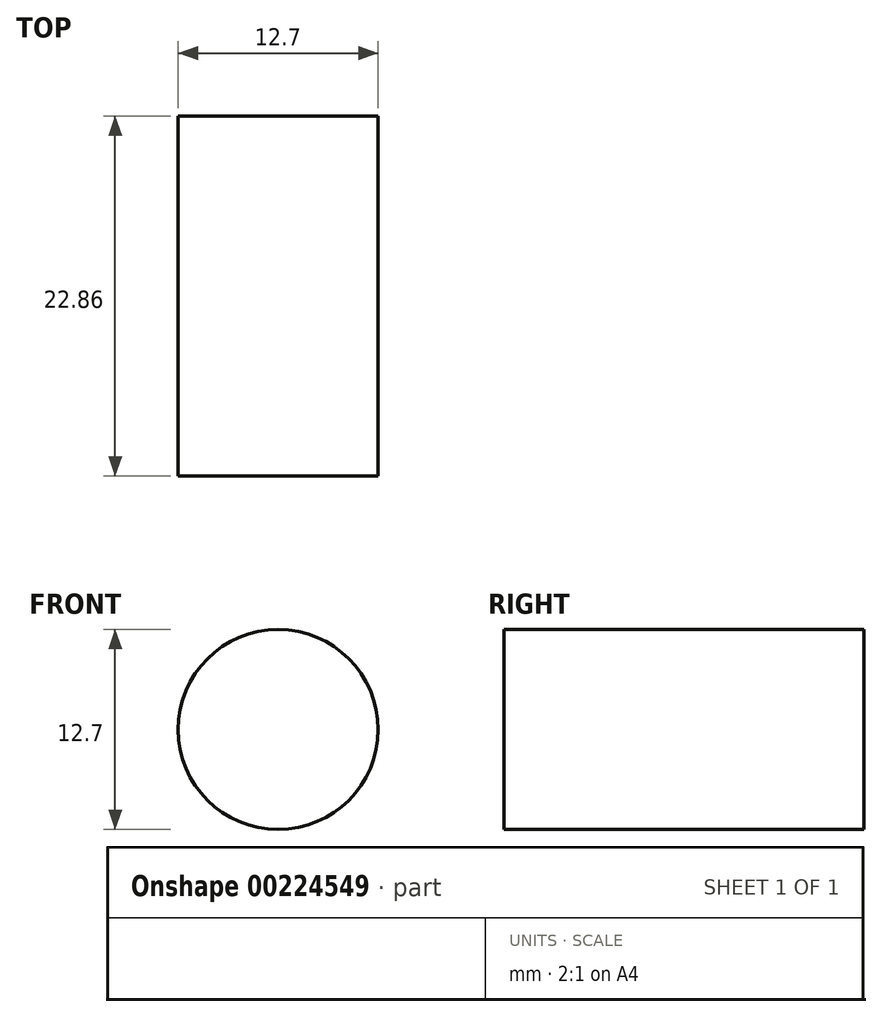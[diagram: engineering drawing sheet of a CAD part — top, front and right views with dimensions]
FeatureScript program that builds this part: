
annotation { "Feature Type Name" : "Feature", "Feature Type Description" : "" }
export const myFeature = defineFeature(function(context is Context, id is Id, definition is map)
    precondition{}
    {
        {
            var Q0;
            Q0=qCreatedBy(makeId("Front.planeOp"),FACE);
            var sketch = newSketch(context, id + "F0", { "sketchPlane" : qUnion([Q0])});
            skCircle(sketch, "E0", {"center": v(-46.2, 33.52) * mm, "radius": 6.35 * mm});
            skSolve(sketch);
        }
        {
            var Q0;
            Q0=makeQuery(id+"F0.imprint","IMPRINT",FACE,{"disambiguationData":[TD([[makeQuery(id+"F0.imprint","IMPRINT",EDGE,{"derivedFrom":sQuery(id+"F0.wireOp",EDGE,"E0")}),1.0]])]});
            extrude(context, id + "F1", {"entities" : qUnion([Q0]), "depth" : 22.86 * mm});
        }
    });
